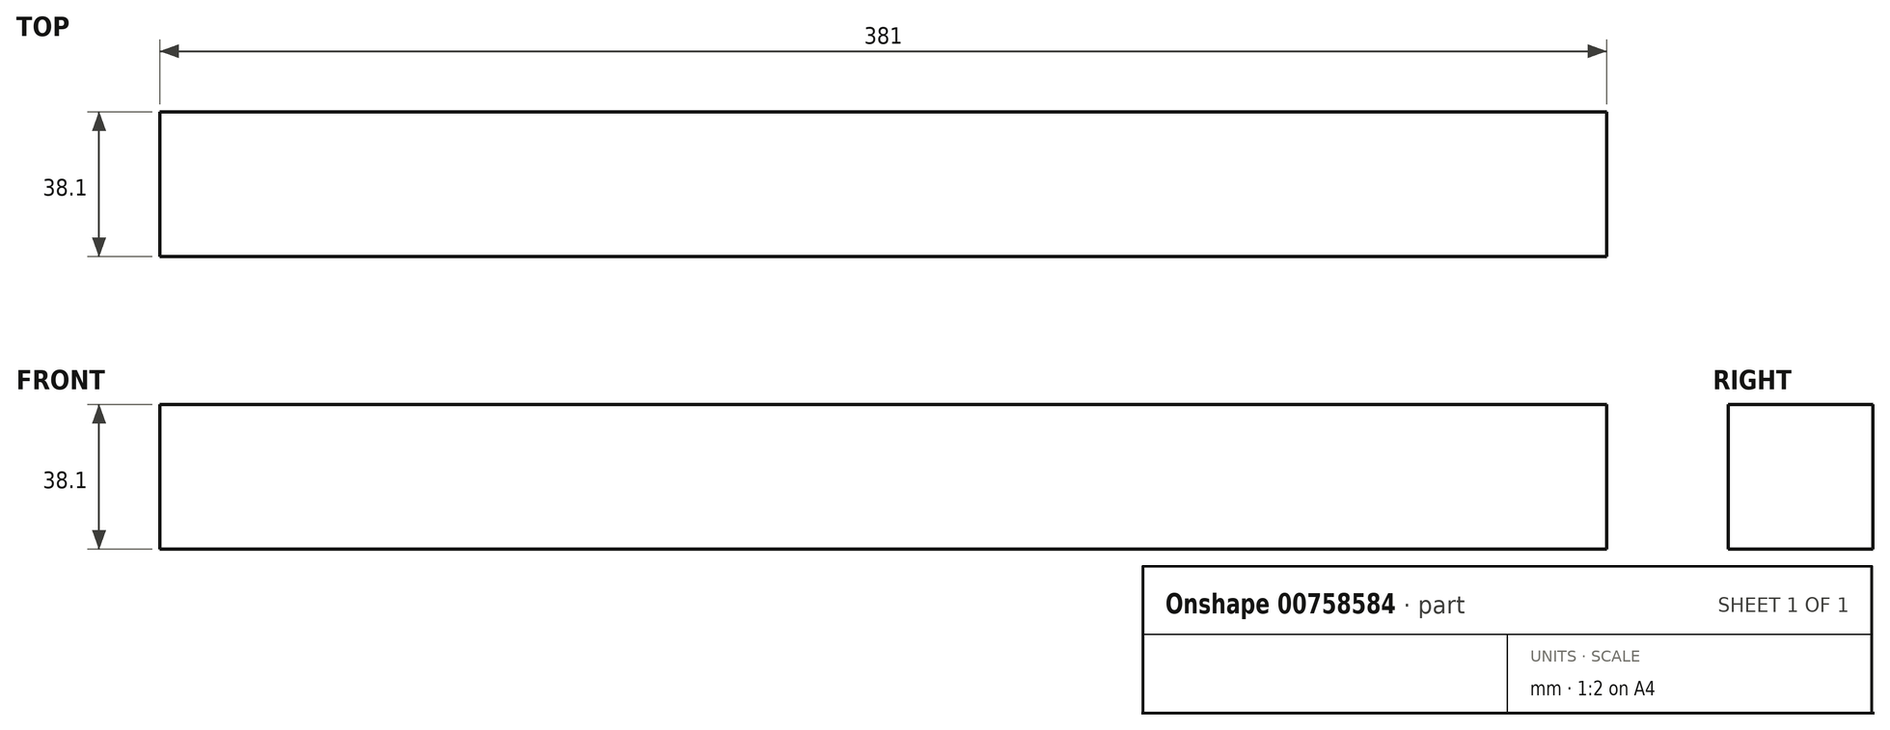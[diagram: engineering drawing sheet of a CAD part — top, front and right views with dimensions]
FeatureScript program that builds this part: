
annotation { "Feature Type Name" : "Feature", "Feature Type Description" : "" }
export const myFeature = defineFeature(function(context is Context, id is Id, definition is map)
    precondition{}
    {
        {
            var Q0;
            Q0=qCreatedBy(makeId("Front.planeOp"),FACE);
            var sketch = newSketch(context, id + "F0", { "sketchPlane" : qUnion([Q0])});
            skLineSegment(sketch, "E0.bottom", {"start": v(-190.5, 19.05) * mm, "end": v(190.5, 19.05) * mm});
            skLineSegment(sketch, "E0.top", {"start": v(-190.5, -19.05) * mm, "end": v(190.5, -19.05) * mm});
            skLineSegment(sketch, "E0.left", {"start": v(-190.5, 19.05) * mm, "end": v(-190.5, -19.05) * mm});
            skLineSegment(sketch, "E0.right", {"start": v(190.5, 19.05) * mm, "end": v(190.5, -19.05) * mm});
            skPoint(sketch, "E0.middle", {"position": v(0, 0) * mm});
            skSolve(sketch);
        }
        {
            var Q0;
            Q0=makeQuery(id+"F0.imprint","IMPRINT",FACE,{"disambiguationData":[TD([[makeQuery(id+"F0.imprint","IMPRINT",EDGE,{"derivedFrom":sQuery(id+"F0.wireOp",EDGE,"E0.bottom")}),-1.0]])]});
            extrude(context, id + "F1", {"entities" : qUnion([Q0]), "endBound" : BoundingType.SYMMETRIC, "depth" : 38.1 * mm, "offsetDistance" : 25.4 * mm});
        }
    });
